MODEL slx_6b8280a9405f
KIND model
CONFIG AbsTol = auto
CONFIG EnableMultiTasking = off
CONFIG FixedStep = SimIn.Environment.Turbulence.dT
CONFIG MaxStep = auto
CONFIG MinStep = auto
CONFIG RelTol = 1e-6
CONFIG SampleTimeConstraint = Unconstrained
CONFIG SolverName = FixedStepAuto
CONFIG StartTime = 0.0
CONFIG StopTime = SimIn.stopTime
BLOCK [SubSystem] Assertions
BLOCK [Clock] Assertions/Clock1
BLOCK [Reference] Assertions/Compare To Constant  REF=simulink/Logic and Bit
Operations/Compare
To Constant
  SourceBlock = simulink/Logic and Bit\nOperations/Compare\nTo Constant
  SourceType = Compare To Constant
BLOCK [Constant] Assertions/Constant2
  Value = SimIn.Switches.TrimModeOn
BLOCK [Constant] Assertions/Constant3
  Value = SimIn.Switches.LinearizeModeOn
BLOCK [Assertion] Assertions/KillifNotSimMode
  AssertionFailFcn = warndlg('Running simulation with TrimMode or LinearizeMode engaged.  Run setup.m to reset.','Warning!')
BLOCK [Logic] Assertions/Logical Operator
  AllPortsSameDT = off
  Operator = NAND
  OutDataTypeStr = boolean
BLOCK [Logic] Assertions/Logical Operator1
  AllPortsSameDT = off
  Operator = OR
  OutDataTypeStr = boolean
BLOCK [BusCreator] Bus Creator
  DisplayOption = bar
  InheritFromInputs = on
  Inputs = 2
  OutDataTypeStr = Bus: BUS_TRIM_INPUT
BLOCK [BusSelector] Bus Selector
  OutputSignals = Vehicle.EOM
BLOCK [BusSelector] Bus Selector1
  OutputAsBus = on
  OutputSignals = AirRelativeData.Veas,AirRelativeData.Vtot,AirRelativeData.alpha,AirRelativeData.beta,WorldRelativeData.gamma,WorldRelativeData.chi,InertialData.Asensed_bIb,AirRelativeData.Vtotdot,AirRelativeData.alphadot,AirRelativeData.betadot,WorldRelativeData.gammadot,WorldRelativeData.chidot,WorldRelativeData.VelDtH_bEh,WorldRelativeData.Euler.phi,WorldRelativeData.Euler.theta,WorldRelativeData.Euler.psi
BLOCK [BusSelector] Bus Selector2
  OutputSignals = InertialData.Pos_bii
BLOCK [BusToVector] Bus to Vector
BLOCK [Demux] Demux
  Outputs = [SimIn.Trim.numEngines SimIn.Trim.numSurfaces]
BLOCK [From] From
  GotoTag = TrimInputs
BLOCK [From] From1
  GotoTag = RefInputs
BLOCK [From] From2
  GotoTag = SimOutputs
BLOCK [From] From3
  GotoTag = EOM
BLOCK [From] From4
  GotoTag = Pos_bii
BLOCK [SubSystem] GenCtrl Inputs
  Variant = on
  VariantControl = Variant1
BLOCK [SubSystem] GenCtrl Inputs/GL-10 Reference Inputs
  ReferencedSubsystem = GL_10_Reference_Inputs
  VariantControl = GVS_VEH_TYPE_GL10
BLOCK [SubSystem] GenCtrl Inputs/Generic Tilt Rotor Reference Inputs
  ReferencedSubsystem = GTR_Reference_Inputs
  VariantControl = GVS_VEH_TYPE_GTR
BLOCK [SubSystem] GenCtrl Inputs/Generic Tilt Wing Reference Inputs
  ReferencedSubsystem = GTW_Reference_Inputs
  VariantControl = GVS_VEH_TYPE_GTW
BLOCK [SubSystem] GenCtrl Inputs/LA-8 Reference Inputs
  ReferencedSubsystem = LA_8_Reference_Inputs
  VariantControl = GVS_VEH_TYPE_LA8
BLOCK [SubSystem] GenCtrl Inputs/Lift+Cruise Reference Inputs
  ReferencedSubsystem = Lift_Cruise_Reference_Inputs
  VariantControl = GVS_VEH_TYPE_LC
BLOCK [Inport] GenCtrl Inputs/Pos_In
BLOCK [SubSystem] GenCtrl Inputs/Quad6 Reference Inputs
  ReferencedSubsystem = Quad6_Reference_Inputs
  VariantControl = GVS_VEH_TYPE_QUAD6
BLOCK [Outport] GenCtrl Inputs/RefInputs
  OutDataTypeStr = Bus: BUS_REF_INPUT
BLOCK [SubSystem] Global Definitions
BLOCK [Constant] Global Definitions/EOM_IC
  OutDataTypeStr = Bus: BUS_PARAM_EOM
  Value = SimPar.EOM
BLOCK [From] Global Definitions/From
  GotoTag = IC
  TagVisibility = global
BLOCK [From] Global Definitions/From1
  GotoTag = EOM_IC
  TagVisibility = global
BLOCK [Goto] Global Definitions/Goto11
  GotoTag = EOM_IC
  TagVisibility = global
BLOCK [Goto] Global Definitions/Goto3
  GotoTag = IC
  TagVisibility = global
BLOCK [Constant] Global Definitions/IC
  OutDataTypeStr = Bus: BUS_PARAM_IC
  Value = SimPar.IC
BLOCK [Terminator] Global Definitions/Terminator
BLOCK [Terminator] Global Definitions/Terminator1
BLOCK [Goto] Goto
  GotoTag = RefInputs
BLOCK [Goto] Goto1
  GotoTag = SimOutputs
BLOCK [Goto] Goto2
  GotoTag = EOM
BLOCK [Goto] Goto3
  GotoTag = Pos_bii
BLOCK [Goto] Goto4
  GotoTag = TrimInputs
BLOCK [Memory] Memory
BLOCK [Inport] TrimInputs
  SamplingMode = Sample based
  SignalType = real
BLOCK [Outport] TrimOutputs
  OutDataTypeStr = double
  SamplingMode = Sample based
  SignalType = real
  VectorParamsAs1DForOutWhenUnconnected = off
BLOCK [SubSystem] Vehicle Simulation
  ReferencedSubsystem = VehicleSimulationRef
LINE Assertions/Clock1:1 -> Assertions/Compare To Constant:1
LINE Assertions/Compare To Constant:1 -> Assertions/Logical Operator:2
LINE Assertions/Constant2:1 -> Assertions/Logical Operator1:1
LINE Assertions/Constant3:1 -> Assertions/Logical Operator1:2
LINE Assertions/Logical Operator1:1 -> Assertions/Logical Operator:1
LINE Assertions/Logical Operator:1 -> Assertions/KillifNotSimMode:1
LINE Bus Creator:1 -> Goto4:1
LINE Bus Selector1:1 -> Bus to Vector:1
LINE Bus Selector2:1 -> Memory:1
LINE Bus Selector:1 -> Goto2:1
LINE Bus to Vector:1 -> TrimOutputs:1
LINE Demux:1 -> Bus Creator:1
LINE Demux:2 -> Bus Creator:2
LINE From1:1 -> Vehicle Simulation:1
LINE From2:1 -> Bus Selector:1
NET From3:1 -> Bus Selector1:1, Bus Selector2:1
LINE From4:1 -> GenCtrl Inputs:1
LINE From:1 -> Vehicle Simulation:2
LINE GenCtrl Inputs:1 -> Goto:1
LINE Global Definitions/EOM_IC:1 -> Global Definitions/Goto11:1
LINE Global Definitions/From1:1 -> Global Definitions/Terminator1:1
LINE Global Definitions/From:1 -> Global Definitions/Terminator:1
LINE Global Definitions/IC:1 -> Global Definitions/Goto3:1
LINE Memory:1 -> Goto3:1
LINE TrimInputs:1 -> Demux:1
LINE Vehicle Simulation:1 -> Goto1:1
note: NET lines group one-source signal fan-out (src -> all destinations, sorted); 1:1 wires keep LINE
